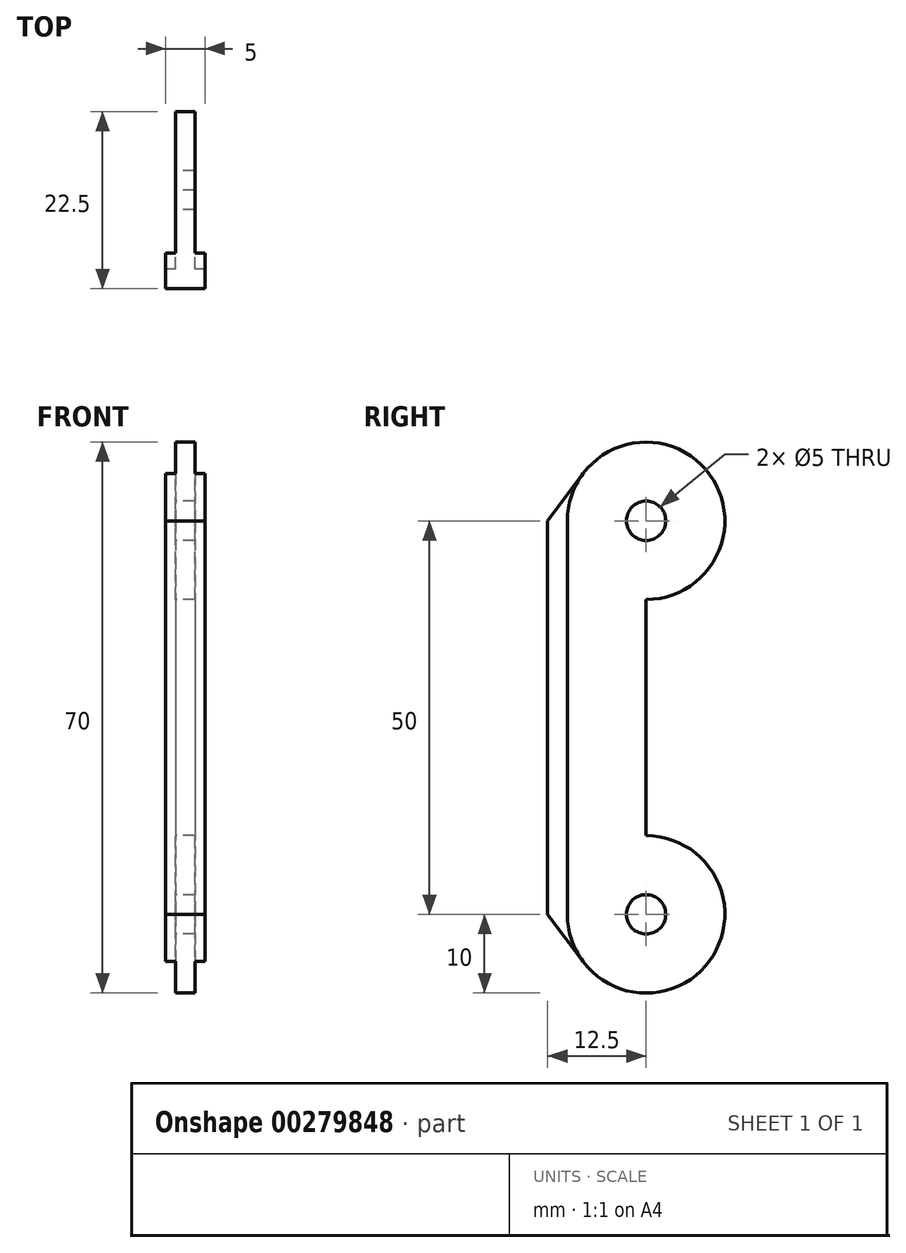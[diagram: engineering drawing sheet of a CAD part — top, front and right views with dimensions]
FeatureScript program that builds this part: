
annotation { "Feature Type Name" : "Feature", "Feature Type Description" : "" }
export const myFeature = defineFeature(function(context is Context, id is Id, definition is map)
    precondition{}
    {
        {
            var Q0;
            Q0=qCreatedBy(makeId("Right.planeOp"),FACE);
            var sketch = newSketch(context, id + "F0", { "sketchPlane" : qUnion([Q0])});
            skCircle(sketch, "E0", {"center": v(0, 25) * mm, "radius": 10 * mm});
            skCircle(sketch, "E1", {"center": v(0, -25) * mm, "radius": 10 * mm});
            skCircle(sketch, "E2", {"center": v(0, 25) * mm, "radius": 2.5 * mm});
            skCircle(sketch, "E3", {"center": v(0, -25) * mm, "radius": 2.5 * mm});
            skLineSegment(sketch, "E4", {"start": v(-10, 25) * mm, "end": v(-10, -25) * mm});
            skLineSegment(sketch, "E5", {"start": v(-12.5, 25) * mm, "end": v(-12.5, -25) * mm});
            skLineSegment(sketch, "E6", {"start": v(0, 15) * mm, "end": v(0, -15) * mm});
            skLineSegment(sketch, "E7", {"start": v(-12.5, 25) * mm, "end": v(-8, 31) * mm});
            skLineSegment(sketch, "E8", {"start": v(-12.5, -25) * mm, "end": v(-8, -31) * mm});
            skLineSegment(sketch, "E9", {"start": v(0, 25) * mm, "end": v(0, 15) * mm, "construction": true});
            skLineSegment(sketch, "E10", {"start": v(0, -15) * mm, "end": v(0, -25) * mm, "construction": true});
            skLineSegment(sketch, "E11", {"start": v(0, 25) * mm, "end": v(-10, 25) * mm, "construction": true});
            skLineSegment(sketch, "E12", {"start": v(0, -25) * mm, "end": v(-10, -25) * mm, "construction": true});
            skLineSegment(sketch, "E13", {"start": v(-10, 25) * mm, "end": v(-12.5, 25) * mm, "construction": true});
            skLineSegment(sketch, "E14", {"start": v(-10, -25) * mm, "end": v(-12.5, -25) * mm, "construction": true});
            skSolve(sketch);
        }
        {
            var Q0;
            {var subQ0=sQuery(id+"F0.wireOp",EDGE,"E4");Q0=makeQuery(id+"F0.imprint","IMPRINT",FACE,{"disambiguationData":[TD([[makeQuery(id+"F0.imprint","IMPRINT",EDGE,{"derivedFrom":subQ0}),-1.0]])]});}
            extrude(context, id + "F1", {"entities" : qUnion([Q0]), "endBound" : BoundingType.SYMMETRIC, "depth" : 5 * mm});
        }
        {
            var Q0;
            Q0=makeQuery(id+"F0.imprint","IMPRINT",FACE,{"disambiguationData":[TD([[makeQuery(id+"F0.imprint","IMPRINT",EDGE,{"derivedFrom":sQuery(id+"F0.wireOp",EDGE,"E2")}),-1.0]])]});
            var Q1;
            {var subQ0=sQuery(id+"F0.wireOp",EDGE,"E4");Q1=makeQuery(id+"F0.imprint","IMPRINT",FACE,{"disambiguationData":[TD([[makeQuery(id+"F0.imprint","IMPRINT",EDGE,{"derivedFrom":subQ0}),1.0]])]});}
            var Q2;
            Q2=makeQuery(id+"F0.imprint","IMPRINT",FACE,{"disambiguationData":[TD([[makeQuery(id+"F0.imprint","IMPRINT",EDGE,{"derivedFrom":sQuery(id+"F0.wireOp",EDGE,"E3")}),-1.0]])]});
            extrude(context, id + "F2", {"entities" : qUnion([Q0, Q1, Q2]), "operationType" : NewBodyOperationType.ADD, "endBound" : BoundingType.SYMMETRIC, "depth" : 2.5 * mm});
        }
    });
